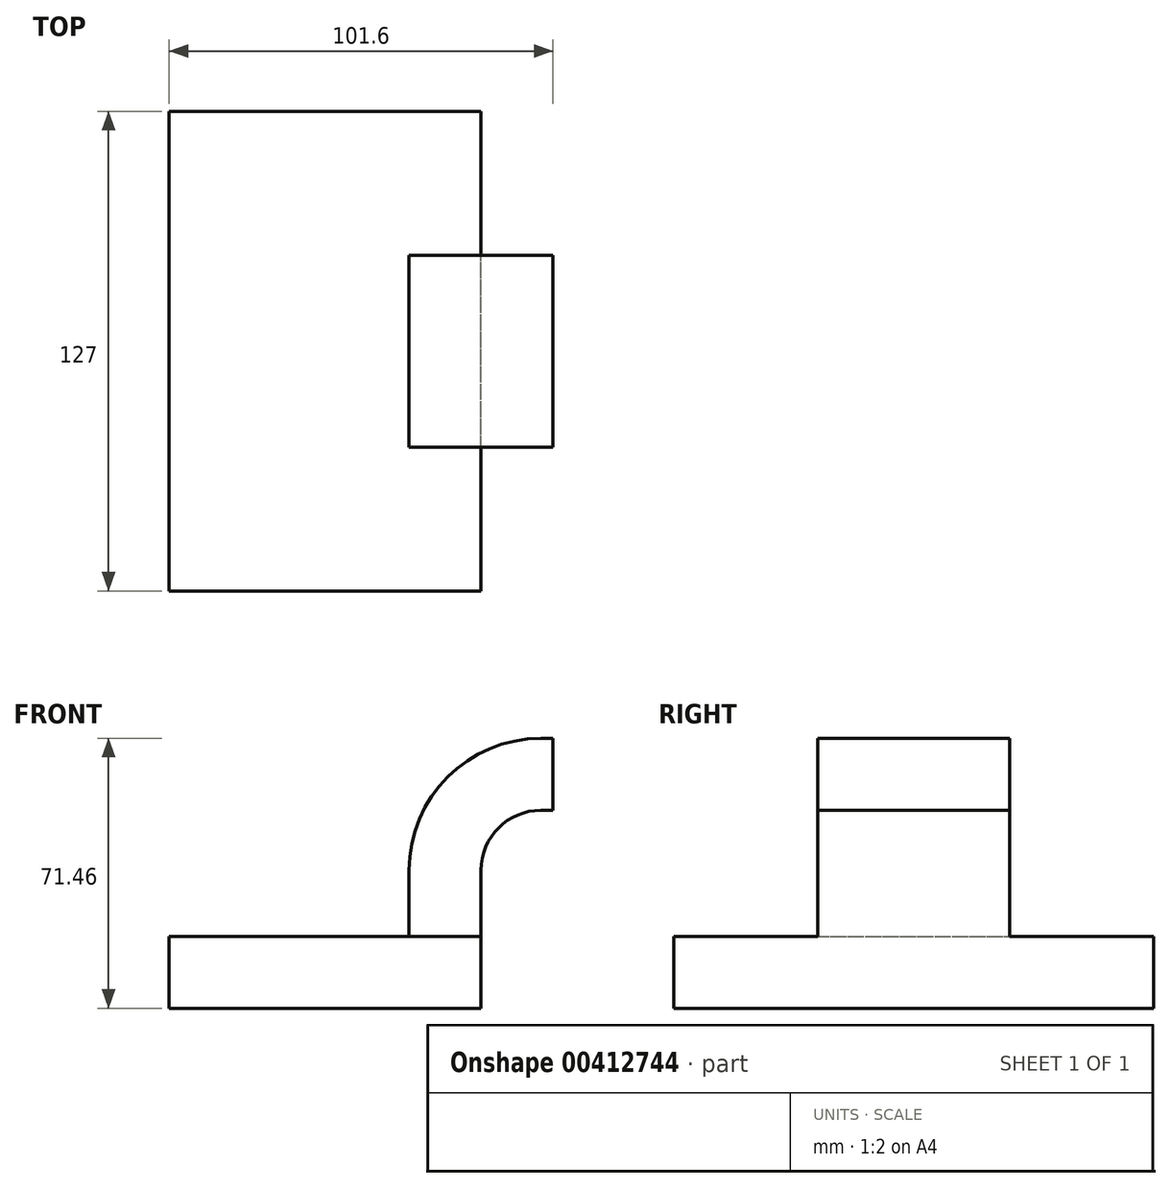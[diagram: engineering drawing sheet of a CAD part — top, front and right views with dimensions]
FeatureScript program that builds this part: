
annotation { "Feature Type Name" : "Feature", "Feature Type Description" : "" }
export const myFeature = defineFeature(function(context is Context, id is Id, definition is map)
    precondition{}
    {
        {
            var Q0;
            Q0=qCreatedBy(makeId("Front.planeOp"),FACE);
            var sketch = newSketch(context, id + "F0", { "sketchPlane" : qUnion([Q0])});
            skLineSegment(sketch, "E0.bottom", {"start": v(41.28, -9.52) * mm, "end": v(-41.28, -9.53) * mm});
            skLineSegment(sketch, "E0.top", {"start": v(41.27, 9.53) * mm, "end": v(-41.28, 9.53) * mm});
            skLineSegment(sketch, "E0.left", {"start": v(41.28, -9.52) * mm, "end": v(41.28, 9.53) * mm});
            skLineSegment(sketch, "E0.right", {"start": v(-41.28, -9.53) * mm, "end": v(-41.28, 9.53) * mm});
            skPoint(sketch, "E0.middle", {"position": v(0, 0) * mm});
            skLineSegment(sketch, "E1.bottom", {"start": v(111.12, 38.1) * mm, "end": v(60.32, 38.1) * mm});
            skLineSegment(sketch, "E1.top", {"start": v(111.12, 66.68) * mm, "end": v(60.32, 66.68) * mm});
            skLineSegment(sketch, "E1.left", {"start": v(111.12, 38.1) * mm, "end": v(111.12, 66.68) * mm});
            skLineSegment(sketch, "E1.right", {"start": v(60.32, 38.1) * mm, "end": v(60.32, 66.68) * mm});
            skPoint(sketch, "E1.middle", {"position": v(85.72, 52.39) * mm});
            skLineSegment(sketch, "E2", {"start": v(41.27, 9.53) * mm, "end": v(41.27, 27) * mm});
            skArc(sketch, "E3", {"start": v(41.28, 27) * mm, "mid": v(45.92, 38.23) * mm, "end": v(57.15, 42.88) * mm});
            skLineSegment(sketch, "E4", {"start": v(57.15, 42.88) * mm, "end": v(85.72, 42.88) * mm});
            skLineSegment(sketch, "E5.0", {"start": v(57.15, 61.93) * mm, "end": v(85.72, 61.93) * mm});
            skArc(sketch, "E5.1", {"start": v(22.23, 27) * mm, "mid": v(32.45, 51.7) * mm, "end": v(57.15, 61.93) * mm});
            skLineSegment(sketch, "E5.2", {"start": v(22.23, 9.53) * mm, "end": v(22.23, 27) * mm});
            skLineSegment(sketch, "E6", {"start": v(85.72, 66.68) * mm, "end": v(85.72, 38.1) * mm});
            skFitSpline(sketch, "E7", {"points": [v(-41.28, 9.53) * mm, v(57.15, 61.93) * mm], "startDerivative": vector(3.52, 45.47) * mm, "endDerivative": vector(121.84, 0) * mm});
            skSolve(sketch);
        }
        {
            var Q0;
            Q0=makeQuery(id+"F0.imprint","IMPRINT",FACE,{"disambiguationData":[TD([[makeQuery(id+"F0.imprint","IMPRINT",EDGE,{"derivedFrom":sQuery(id+"F0.wireOp",EDGE,"E0.bottom")}),-1.0]])]});
            extrude(context, id + "F1", {"entities" : qUnion([Q0]), "endBound" : BoundingType.SYMMETRIC, "depth" : 127 * mm});
        }
        {
            var Q0;
            Q0=makeQuery(id+"F0.imprint","IMPRINT",FACE,{"disambiguationData":[TD([[makeQuery(id+"F0.imprint","IMPRINT",EDGE,{"derivedFrom":sQuery(id+"F0.wireOp",EDGE,"E5.1")}),1.0]])]});
            var Q1;
            {var subQ1=sQuery(id+"F0.wireOp",EDGE,"E2");Q1=makeQuery(id+"F0.imprint","IMPRINT",FACE,{"disambiguationData":[TD([[makeQuery(id+"F0.imprint","IMPRINT",EDGE,{"derivedFrom":subQ1}),1.0]])]});}
            extrude(context, id + "F2", {"entities" : qUnion([Q0, Q1]), "operationType" : NewBodyOperationType.ADD, "endBound" : BoundingType.SYMMETRIC, "depth" : 50.8 * mm});
        }
    });
